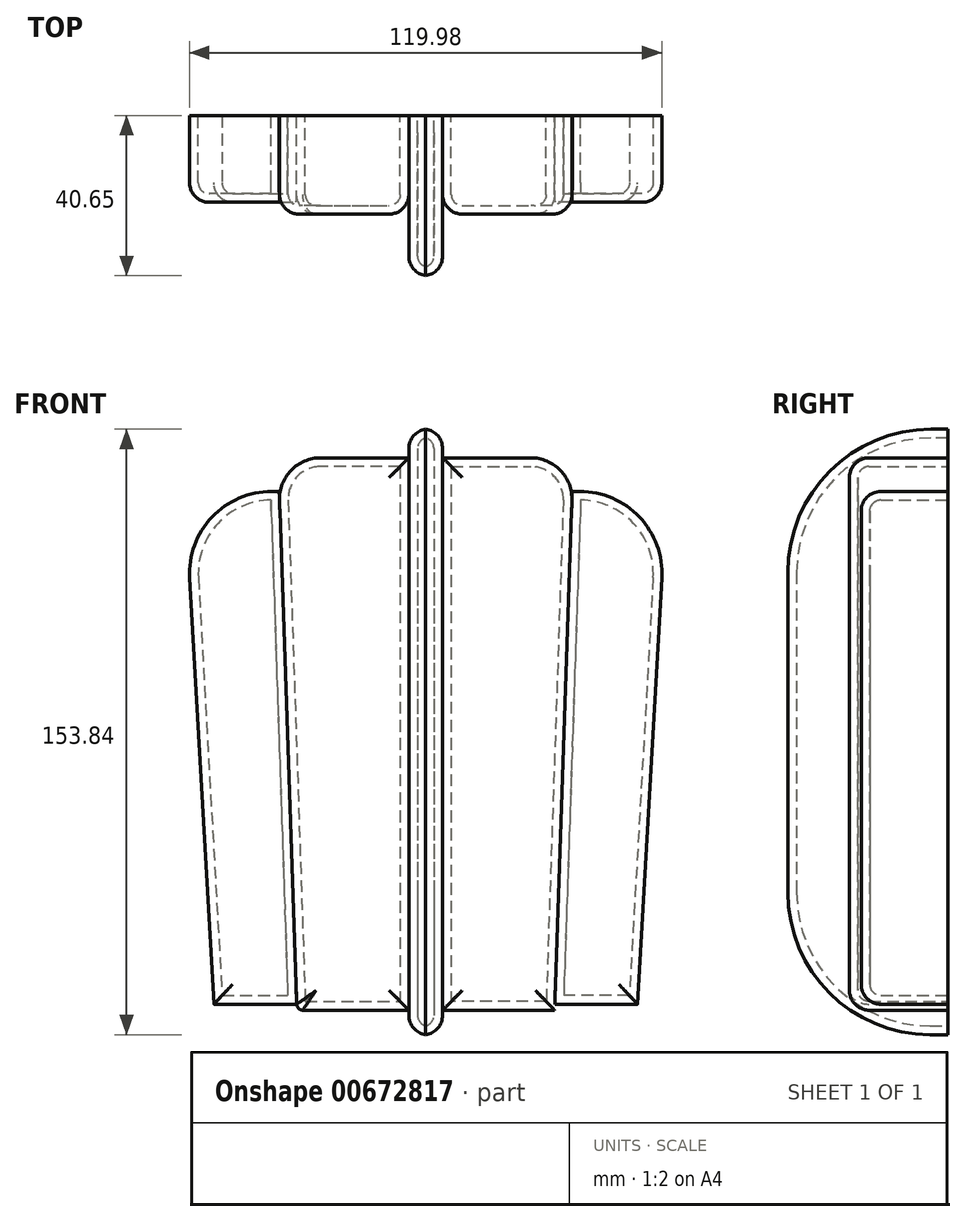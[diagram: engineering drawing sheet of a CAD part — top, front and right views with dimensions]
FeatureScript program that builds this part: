
annotation { "Feature Type Name" : "Feature", "Feature Type Description" : "" }
export const myFeature = defineFeature(function(context is Context, id is Id, definition is map)
    precondition{}
    {
        {
            var Q0;
            Q0=qCreatedBy(makeId("Front.planeOp"),FACE);
            var sketch = newSketch(context, id + "F0", { "sketchPlane" : qUnion([Q0])});
            skLineSegment(sketch, "E0", {"start": v(0, 95.52) * mm, "end": v(-4.28, 95.52) * mm});
            skLineSegment(sketch, "E1", {"start": v(-4.28, 95.52) * mm, "end": v(-4.28, -58.43) * mm});
            skLineSegment(sketch, "E2", {"start": v(-4.28, -58.43) * mm, "end": v(0, -58.43) * mm});
            skLineSegment(sketch, "E3", {"start": v(0, 95.52) * mm, "end": v(0, -58.43) * mm});
            skLineSegment(sketch, "E4.MirrorCS", {"start": v(0, 95.52) * mm, "end": v(4.28, 95.52) * mm});
            skLineSegment(sketch, "E5.MirrorCS", {"start": v(4.28, 95.52) * mm, "end": v(4.28, -58.43) * mm});
            skLineSegment(sketch, "E6.MirrorCS", {"start": v(4.28, -58.43) * mm, "end": v(0, -58.43) * mm});
            skLineSegment(sketch, "E7", {"start": v(-4.28, 88.2) * mm, "end": v(-37.52, 88.2) * mm});
            skLineSegment(sketch, "E8", {"start": v(-37.52, 88.2) * mm, "end": v(-32.73, -52.15) * mm});
            skLineSegment(sketch, "E9", {"start": v(-32.73, -52.15) * mm, "end": v(-4.28, -52.15) * mm});
            skLineSegment(sketch, "E10", {"start": v(-37.23, 79.65) * mm, "end": v(-61.2, 79.65) * mm});
            skLineSegment(sketch, "E11", {"start": v(-61.2, 79.65) * mm, "end": v(-53.83, -50.64) * mm});
            skLineSegment(sketch, "E12", {"start": v(-53.83, -50.64) * mm, "end": v(-32.73, -50.64) * mm});
            skLineSegment(sketch, "E13.MirrorCS", {"start": v(4.28, 88.2) * mm, "end": v(37.52, 88.2) * mm});
            skLineSegment(sketch, "E14.MirrorCS", {"start": v(37.52, 88.2) * mm, "end": v(32.73, -52.15) * mm});
            skLineSegment(sketch, "E15.MirrorCS", {"start": v(32.73, -52.15) * mm, "end": v(4.28, -52.15) * mm});
            skLineSegment(sketch, "E16.MirrorCS", {"start": v(53.84, -50.64) * mm, "end": v(32.73, -50.64) * mm});
            skLineSegment(sketch, "E17.MirrorCS", {"start": v(61.2, 79.65) * mm, "end": v(53.84, -50.64) * mm});
            skLineSegment(sketch, "E18.MirrorCS", {"start": v(37.23, 79.65) * mm, "end": v(61.2, 79.65) * mm});
            skSolve(sketch);
        }
        {
            var Q0;
            {var subQ4=sQuery(id+"F0.wireOp",EDGE,"E17.MirrorCS");Q0=makeQuery(id+"F0.imprint","IMPRINT",FACE,{"disambiguationData":[TD([[makeQuery(id+"F0.imprint","IMPRINT",EDGE,{"derivedFrom":subQ4}),-1.0]])]});}
            extrude(context, id + "F1", {"entities" : qUnion([Q0]), "depth" : 22 * mm, "offsetDistance" : 25 * mm});
        }
        {
            var Q0;
            {var subQ3=sQuery(id+"F0.wireOp",EDGE,"E13.MirrorCS");Q0=makeQuery(id+"F0.imprint","IMPRINT",FACE,{"disambiguationData":[TD([[makeQuery(id+"F0.imprint","IMPRINT",EDGE,{"derivedFrom":subQ3}),-1.0]])]});}
            extrude(context, id + "F2", {"entities" : qUnion([Q0]), "depth" : 25 * mm, "offsetDistance" : 25 * mm});
        }
        {
            var Q0;
            {var subQ0=sQuery(id+"F0.wireOp",EDGE,"E10");Q0=makeQuery(id+"F0.imprint","IMPRINT",FACE,{"disambiguationData":[TD([[makeQuery(id+"F0.imprint","IMPRINT",EDGE,{"derivedFrom":subQ0}),1.0]])]});}
            extrude(context, id + "F3", {"entities" : qUnion([Q0]), "depth" : 22 * mm, "offsetDistance" : 25 * mm});
        }
        {
            var Q0;
            {var subQ3=sQuery(id+"F0.wireOp",EDGE,"E7");Q0=makeQuery(id+"F0.imprint","IMPRINT",FACE,{"disambiguationData":[TD([[makeQuery(id+"F0.imprint","IMPRINT",EDGE,{"derivedFrom":subQ3}),1.0]])]});}
            extrude(context, id + "F4", {"entities" : qUnion([Q0]), "depth" : 25 * mm, "offsetDistance" : 25 * mm});
        }
        {
            var Q0;
            {var subQ4=sQuery(id+"F0.wireOp",EDGE,"E0");Q0=makeQuery(id+"F0.imprint","IMPRINT",FACE,{"disambiguationData":[TD([[makeQuery(id+"F0.imprint","IMPRINT",EDGE,{"derivedFrom":subQ4}),1.0]])]});}
            var Q1;
            Q1=makeQuery(id+"F0.imprint","IMPRINT",FACE,{"disambiguationData":[TD([[makeQuery(id+"F0.imprint","IMPRINT",EDGE,{"derivedFrom":sQuery(id+"F0.wireOp",EDGE,"E3")}),1.0]])]});
            extrude(context, id + "F5", {"entities" : qUnion([Q0, Q1]), "depth" : 40.7 * mm, "offsetDistance" : 25 * mm});
        }
        {
            var Q0;
            Q0=makeQuery(id+"F4.opExtrude","SWEPT_EDGE",EDGE,{"disambiguationData":[OSD([sQuery(id+"F0.wireOp",EDGE,"E7"),sQuery(id+"F0.wireOp",EDGE,"E8")])]});
            fillet(context, id + "F6", {"entities" : qUnion([Q0]), "radius" : 10.48 * mm, "tangentPropagation" : true, "allowEdgeOverflow" : false});
        }
        {
            var Q0;
            Q0=makeQuery(id+"F3.opExtrude","SWEPT_EDGE",EDGE,{"disambiguationData":[OSD([sQuery(id+"F0.wireOp",EDGE,"E10"),sQuery(id+"F0.wireOp",EDGE,"E11")])]});
            fillet(context, id + "F7", {"entities" : qUnion([Q0]), "radius" : 20.84 * mm, "tangentPropagation" : true, "allowEdgeOverflow" : false});
        }
        {
            var Q0;
            Q0=makeQuery(id+"F3.opExtrude","SWEPT_EDGE",EDGE,{"disambiguationData":[OSD([sQuery(id+"F0.wireOp",EDGE,"E11"),sQuery(id+"F0.wireOp",EDGE,"E12")])]});
            fillet(context, id + "F8", {"entities" : qUnion([Q0]), "radius" : 0.03 * mm, "tangentPropagation" : true, "allowEdgeOverflow" : false});
        }
        {
            var Q0;
            Q0=makeQuery(id+"F2.opExtrude","SWEPT_EDGE",EDGE,{"disambiguationData":[OSD([sQuery(id+"F0.wireOp",EDGE,"E13.MirrorCS"),sQuery(id+"F0.wireOp",EDGE,"E14.MirrorCS")])]});
            fillet(context, id + "F9", {"entities" : qUnion([Q0]), "radius" : 10.48 * mm, "tangentPropagation" : true, "allowEdgeOverflow" : false});
        }
        {
            var Q0;
            Q0=makeQuery(id+"F1.opExtrude","SWEPT_EDGE",EDGE,{"disambiguationData":[OSD([sQuery(id+"F0.wireOp",EDGE,"E16.MirrorCS"),sQuery(id+"F0.wireOp",EDGE,"E17.MirrorCS")])]});
            fillet(context, id + "F10", {"entities" : qUnion([Q0]), "radius" : 0.03 * mm, "tangentPropagation" : true, "allowEdgeOverflow" : false});
        }
        {
            var Q0;
            Q0=makeQuery(id+"F1.opExtrude","SWEPT_EDGE",EDGE,{"disambiguationData":[OSD([sQuery(id+"F0.wireOp",EDGE,"E17.MirrorCS"),sQuery(id+"F0.wireOp",EDGE,"E18.MirrorCS")])]});
            fillet(context, id + "F11", {"entities" : qUnion([Q0]), "radius" : 20.84 * mm, "tangentPropagation" : true, "allowEdgeOverflow" : false});
        }
        {
            var Q0;
            Q0=makeQuery(id+"F5.opExtrude","CAP_EDGE",EDGE,{"disambiguationData":[OSD([sQuery(id+"F0.wireOp",EDGE,"E0"),sQuery(id+"F0.wireOp",EDGE,"E4.MirrorCS")])],"isStart":false});
            fillet(context, id + "F12", {"entities" : qUnion([Q0]), "radius" : 36.45 * mm, "tangentPropagation" : true, "allowEdgeOverflow" : false});
        }
        {
            var Q0;
            Q0=makeQuery(id+"F5.opExtrude","CAP_EDGE",EDGE,{"disambiguationData":[OSD([sQuery(id+"F0.wireOp",EDGE,"E2"),sQuery(id+"F0.wireOp",EDGE,"E6.MirrorCS")])],"isStart":false});
            fillet(context, id + "F13", {"entities" : qUnion([Q0]), "radius" : 36.2 * mm, "tangentPropagation" : true, "allowEdgeOverflow" : false});
        }
        {
            var Q0;
            Q0=makeQuery(id+"F12.opFillet","BLEND_FACE",FACE,{"disambiguationData":[OSD([sQuery(id+"F0.wireOp",EDGE,"E0"),sQuery(id+"F0.wireOp",EDGE,"E4.MirrorCS")])]});
            fillet(context, id + "F14", {"entities" : qUnion([Q0]), "radius" : 5 * mm, "tangentPropagation" : true, "allowEdgeOverflow" : false});
        }
        {
            var Q0;
            Q0=makeQuery(id+"F4.opExtrude","CAP_FACE",FACE,{"disambiguationData":[OSD([sQuery(id+"F0.wireOp",EDGE,"E1"),sQuery(id+"F0.wireOp",EDGE,"E7"),sQuery(id+"F0.wireOp",EDGE,"E8"),sQuery(id+"F0.wireOp",EDGE,"E9")])],"isStart":false});
            fillet(context, id + "F15", {"entities" : qUnion([Q0]), "radius" : 5 * mm, "tangentPropagation" : true, "allowEdgeOverflow" : false});
        }
        {
            var Q0;
            Q0=makeQuery(id+"F3.opExtrude","CAP_EDGE",EDGE,{"disambiguationData":[OSD([sQuery(id+"F0.wireOp",EDGE,"E12")])],"isStart":false});
            fillet(context, id + "F16", {"entities" : qUnion([Q0]), "radius" : 5 * mm, "tangentPropagation" : true, "allowEdgeOverflow" : false});
        }
        {
            var Q0;
            Q0=makeQuery(id+"F2.opExtrude","CAP_FACE",FACE,{"disambiguationData":[OSD([sQuery(id+"F0.wireOp",EDGE,"E5.MirrorCS"),sQuery(id+"F0.wireOp",EDGE,"E13.MirrorCS"),sQuery(id+"F0.wireOp",EDGE,"E14.MirrorCS"),sQuery(id+"F0.wireOp",EDGE,"E15.MirrorCS")])],"isStart":false});
            fillet(context, id + "F17", {"entities" : qUnion([Q0]), "radius" : 5 * mm, "tangentPropagation" : true, "allowEdgeOverflow" : false});
        }
        {
            var Q0;
            Q0=makeQuery(id+"F1.opExtrude","CAP_EDGE",EDGE,{"disambiguationData":[OSD([sQuery(id+"F0.wireOp",EDGE,"E16.MirrorCS")])],"isStart":false});
            fillet(context, id + "F18", {"entities" : qUnion([Q0]), "radius" : 5 * mm, "tangentPropagation" : true, "allowEdgeOverflow" : false});
        }
        {
            var Q0;
            Q0=makeQuery(id+"F1.opExtrude","CAP_FACE",FACE,{"disambiguationData":[OSD([sQuery(id+"F0.wireOp",EDGE,"E14.MirrorCS"),sQuery(id+"F0.wireOp",EDGE,"E16.MirrorCS"),sQuery(id+"F0.wireOp",EDGE,"E17.MirrorCS"),sQuery(id+"F0.wireOp",EDGE,"E18.MirrorCS")])],"isStart":true});
            var Q1;
            Q1=makeQuery(id+"F2.opExtrude","CAP_FACE",FACE,{"disambiguationData":[OSD([sQuery(id+"F0.wireOp",EDGE,"E5.MirrorCS"),sQuery(id+"F0.wireOp",EDGE,"E13.MirrorCS"),sQuery(id+"F0.wireOp",EDGE,"E14.MirrorCS"),sQuery(id+"F0.wireOp",EDGE,"E15.MirrorCS")])],"isStart":true});
            var Q2;
            Q2=makeQuery(id+"F5.opExtrude","CAP_FACE",FACE,{"disambiguationData":[OSD([sQuery(id+"F0.wireOp",EDGE,"E0"),sQuery(id+"F0.wireOp",EDGE,"E1"),sQuery(id+"F0.wireOp",EDGE,"E2"),sQuery(id+"F0.wireOp",EDGE,"E4.MirrorCS"),sQuery(id+"F0.wireOp",EDGE,"E5.MirrorCS"),sQuery(id+"F0.wireOp",EDGE,"E6.MirrorCS")])],"isStart":true});
            var Q3;
            Q3=makeQuery(id+"F4.opExtrude","CAP_FACE",FACE,{"disambiguationData":[OSD([sQuery(id+"F0.wireOp",EDGE,"E1"),sQuery(id+"F0.wireOp",EDGE,"E7"),sQuery(id+"F0.wireOp",EDGE,"E8"),sQuery(id+"F0.wireOp",EDGE,"E9")])],"isStart":true});
            var Q4;
            Q4=makeQuery(id+"F3.opExtrude","CAP_FACE",FACE,{"disambiguationData":[OSD([sQuery(id+"F0.wireOp",EDGE,"E8"),sQuery(id+"F0.wireOp",EDGE,"E10"),sQuery(id+"F0.wireOp",EDGE,"E11"),sQuery(id+"F0.wireOp",EDGE,"E12")])],"isStart":true});
            shell(context, id + "F19", {"entities" : qUnion([Q0, Q1, Q2, Q3, Q4]), "thickness" : 2.2 * mm});
        }
        {
            var Q0;
            Q0=makeQuery(id+"F4.opExtrude","SWEPT_EDGE",EDGE,{"disambiguationData":[OSD([sQuery(id+"F0.wireOp",EDGE,"E8"),sQuery(id+"F0.wireOp",EDGE,"E9")])]});
            fillet(context, id + "F20", {"entities" : qUnion([Q0]), "radius" : 1.56 * mm, "tangentPropagation" : true, "allowEdgeOverflow" : false});
        }
    });
